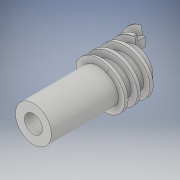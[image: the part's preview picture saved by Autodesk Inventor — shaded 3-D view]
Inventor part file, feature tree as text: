
AUTODESK INVENTOR PART (.ipt)
format: ipt  version: 2018 (Build 220112000, 112)  size: 498,688 bytes
history: native  units: in
note: dims shown in document units (in); Inventor stores cm internally (conversion verified against a paired STEP export)
features: sketch x10, extrude x5, helix x3, other x2, hole x2, plane x1, loft x1, projected_geometry x1
ambient origin geometry x8: Origin, YZ Plane, XZ Plane, XY Plane, X Axis, Y Axis, Z Axis, Center Point
bodies: Solid1 (feature_tree)
feature tree (25):
  sketch  "Sketch1"  dims[d0=2.0in d2=3.9in]
  plane  "Work Plane1"
  sketch  "Sketch2"  dims[d3=0.5in d5=0.0in d6=90.0deg d7=0.0in d8=90.0deg]
  loft  "Loft1"
  other  "Work Point1"
  hole  "Hole1"  [1 undecoded]
  other  "Work Axis2"
  sketch  "Sketch6"  dims[d110=1.0in d111=1.0in d11=0.185in d12=0.75in d13=0.375in d14=0.25in d15=0.5635in d16=1.0in d17=0.8108in d41=0.1in]
  helix  "Coil3"  [1 undecoded]
  helix  "Coil4"  [1 undecoded]
  sketch  "Sketch8"  dims[d42=0.1in d43=0.02in]
  extrude  "Extrusion2"  Depth=0.02in
  helix  "Coil5"  [1 undecoded]
  extrude  "Extrusion3"  Depth=0.1in
  extrude  "Extrusion4"  Depth=0.1in
  sketch  "Sketch12"  dims[d67=0.02in d68=0.1in]
  hole  "Hole2"  [1 undecoded]
  extrude  "Extrusion5"  Depth=0.185in
  extrude  "Extrusion6"  Depth=0.185in TaperAngle=0.0deg
  projected_geometry  "Projected Loop1"
  sketch  "Sketch9"  dims[d44=0.13in d45=1.0in d46=11.811in d47=-0.0739in d48=90.0deg d49=90.0deg d50=0.0in d51=0.0in]
  sketch  "Sketch10"  dims[d52=0.13in d53=1.0in d54=11.811in d55=0.0756in d56=90.0deg d57=90.0deg d58=0.0in d59=0.0in d60=3.775in]
  sketch  "Sketch11"  dims[d63=3.25in d64=0.0in d66=0.1in]
  sketch  "Sketch13"  dims[d69=0.185in d70=0.13in]
  sketch  "Sketch14"  dims[d71=0.5436in d72=0.13in d73=1.0in d74=1.5748in d75=0.0in d76=90.0deg d77=90.0deg d78=0.0in d79=0.0in d80=0.37in d81=0.3in d82=0.0in d83=1.0in d84=0.0in d86=0.02in d87=0.0in d88=0.125in d89=3.0in d90=0.0in d91=0.0in d92=0.5in d108=1.0in d109=1.0in d95=0.185in d96=0.75in d97=0.375in d98=0.25in d99=0.5635in d100=1.0in d101=0.8108in d102=3.4375in d103=0.065in d104=2.87in d105=0.0in d106=2.2in d107=0.0in]
note: 5 required parameter values undecoded (feature->parameter linkage not recoverable at this tier; creation-order binding heuristic only, values carry confidence <= 0.55)
